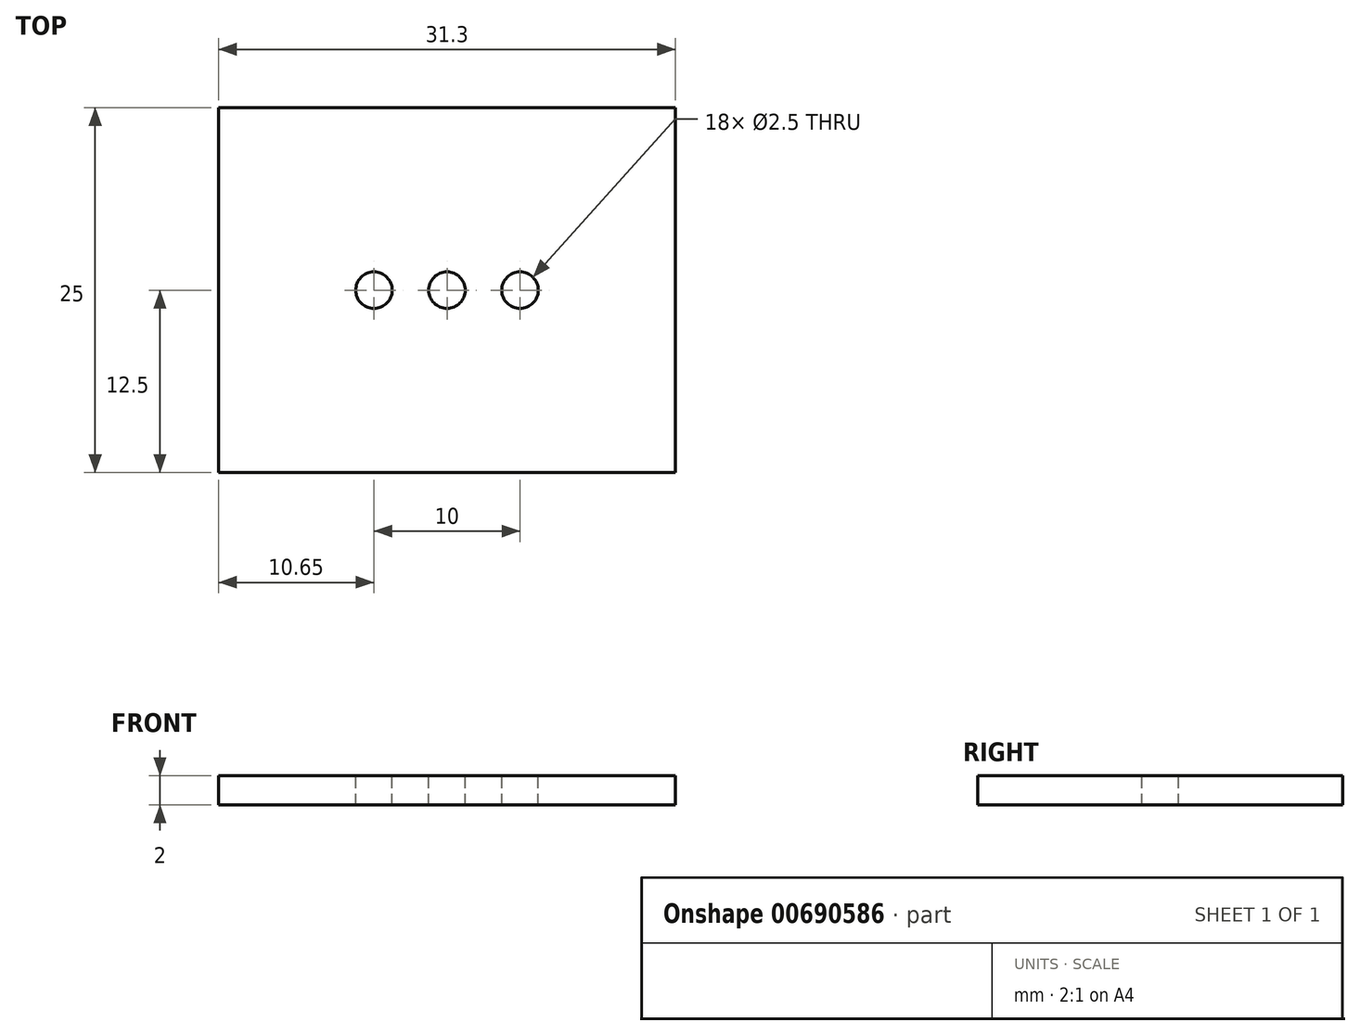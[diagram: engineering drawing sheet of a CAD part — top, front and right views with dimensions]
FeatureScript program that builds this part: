
annotation { "Feature Type Name" : "Feature", "Feature Type Description" : "" }
export const myFeature = defineFeature(function(context is Context, id is Id, definition is map)
    precondition{}
    {
        {
            var Q0;
            Q0=qCreatedBy(makeId("Front.planeOp"),FACE);
            var sketch = newSketch(context, id + "F0", { "sketchPlane" : qUnion([Q0])});
            skLineSegment(sketch, "E0.bottom", {"start": v(0, 0) * mm, "end": v(31.3, 0) * mm});
            skLineSegment(sketch, "E0.top", {"start": v(0, 2) * mm, "end": v(31.3, 2) * mm});
            skLineSegment(sketch, "E0.left", {"start": v(0, 0) * mm, "end": v(0, 2) * mm});
            skLineSegment(sketch, "E0.right", {"start": v(31.3, 0) * mm, "end": v(31.3, 2) * mm});
            skSolve(sketch);
        }
        {
            var Q0;
            Q0 = qSketchRegion(id + "F0", true);
            extrude(context, id + "F1", {"entities" : qUnion([Q0]), "depth" : 25 * mm, "offsetDistance" : 25 * mm});
        }
        {
            var Q0;
            Q0=makeQuery(id+"F1.opExtrude","SWEPT_FACE",FACE,{"disambiguationData":[OSD([sQuery(id+"F0.wireOp",EDGE,"E0.top")])]});
            var sketch = newSketch(context, id + "F2", { "sketchPlane" : qUnion([Q0])});
            skLineSegment(sketch, "E1", {"start": v(0, -12.5) * mm, "end": v(31.3, -12.5) * mm, "construction": true});
            skPoint(sketch, "E2", {"position": v(15.65, -12.5) * mm});
            skPoint(sketch, "E3", {"position": v(20.65, -12.5) * mm});
            skPoint(sketch, "E4", {"position": v(10.65, -12.5) * mm});
            skSolve(sketch);
        }
        {
            var Q0;
            Q0=sQuery(id+"F2.wireOp",VERTEX,"E4");
            var Q1;
            Q1=sQuery(id+"F2.wireOp",VERTEX,"E2");
            var Q2;
            Q2=sQuery(id+"F2.wireOp",VERTEX,"E3");
            var Q3;
            Q3=makeQuery(id+"F1.opExtrude","SWEPT_BODY",BODY,{"disambiguationData":[OSD([sQuery(id+"F0.wireOp",EDGE,"E0.bottom"),sQuery(id+"F0.wireOp",EDGE,"E0.top"),sQuery(id+"F0.wireOp",EDGE,"E0.left"),sQuery(id+"F0.wireOp",EDGE,"E0.right")])]});
            hole(context, id + "F3", {"style" : HoleStyle.SIMPLE, "endStyle" : HoleEndStyle.THROUGH, "holeDiameter" : 2.5 * mm, "majorDiameter" : 5 * mm, "isTappedThrough" : true, "tappedDepth" : 12 * mm, "tapClearance" : 3, "locations" : qUnion([Q0, Q1, Q2]), "scope" : qUnion([Q3])});
        }
    });
